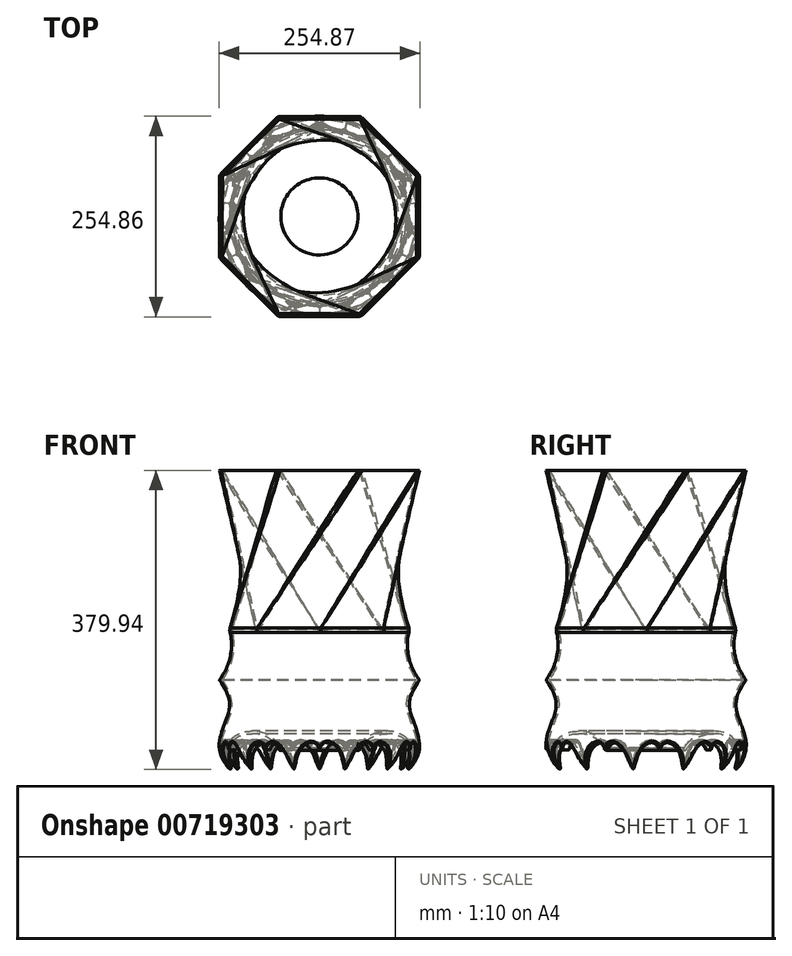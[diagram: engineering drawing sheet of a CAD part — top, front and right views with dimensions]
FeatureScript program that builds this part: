
annotation { "Feature Type Name" : "Feature", "Feature Type Description" : "" }
export const myFeature = defineFeature(function(context is Context, id is Id, definition is map)
    precondition{}
    {
        {
            var Q0;
            Q0=qCreatedBy(makeId("Front.planeOp"),FACE);
            var sketch = newSketch(context, id + "F0", { "sketchPlane" : qUnion([Q0])});
            skLineSegment(sketch, "E0", {"start": v(-49.67, 0) * mm, "end": v(1.13, 0) * mm});
            skLineSegment(sketch, "E1", {"start": v(-49.67, 0) * mm, "end": v(-49.67, 88.9) * mm});
            skLineSegment(sketch, "E2", {"start": v(-49.67, 88.9) * mm, "end": v(77.33, 88.9) * mm});
            skFitSpline(sketch, "E3", {"points": [v(77.33, 88.9) * mm, v(69.32, 37.63) * mm, v(77.33, 0) * mm, v(60.87, -29.47) * mm], "startDerivative": vector(-145.93, -197.22) * mm, "endDerivative": vector(-71.47, -73.7) * mm});
            skFitSpline(sketch, "E4", {"points": [v(1.13, 0) * mm, v(20.7, 18.23) * mm, v(52.43, 17.54) * mm, v(65.67, 0) * mm, v(60.87, -29.47) * mm], "startDerivative": vector(49.37, 90.75) * mm, "endDerivative": vector(-45.51, -125.15) * mm});
            skLineSegment(sketch, "E5", {"start": v(-49.67, 88.9) * mm, "end": v(-49.67, 152.4) * mm});
            skLineSegment(sketch, "E6", {"start": v(-49.67, 152.4) * mm, "end": v(64.63, 152.4) * mm});
            skFitSpline(sketch, "E7", {"points": [v(64.63, 152.4) * mm, v(64.63, 114.98) * mm, v(77.33, 88.9) * mm], "startDerivative": vector(-25.46, -92) * mm, "endDerivative": vector(52.49, -80.1) * mm});
            skSolve(sketch);
        }
        {
            var Q0;
            Q0=makeQuery(id+"F0.imprint","IMPRINT",FACE,{"disambiguationData":[TD([[makeQuery(id+"F0.imprint","IMPRINT",EDGE,{"derivedFrom":sQuery(id+"F0.wireOp",EDGE,"E0")}),1.0]])]});
            var Q1;
            Q1=makeQuery(id+"F0.imprint","IMPRINT",FACE,{"disambiguationData":[TD([[makeQuery(id+"F0.imprint","IMPRINT",EDGE,{"derivedFrom":sQuery(id+"F0.wireOp",EDGE,"E2")}),1.0]])]});
            var Q2;
            Q2=sQuery(id+"F0.wireOp",EDGE,"E1");
            revolve(context, id + "F1", {"surfaceOperationType" : NewSurfaceOperationType.NEW, "entities" : qUnion([Q0, Q1]), "axis" : qUnion([Q2]), "revolveType" : RevolveType.FULL});
        }
        {
            var Q0;
            Q0=qCreatedBy(makeId("Front.planeOp"),FACE);
            cPlane(context, id + "F2", {"entities" : qUnion([Q0]), "cplaneType" : CPlaneType.OFFSET, "offset" : 228.6 * mm, "width" : 152.4 * mm, "height" : 152.4 * mm});
        }
        {
            var Q0;
            Q0=qCreatedBy(id+"F2.planeOp",FACE);
            var sketch = newSketch(context, id + "F3", { "sketchPlane" : qUnion([Q0])});
            skLineSegment(sketch, "E8", {"start": v(-49.7, 40.01) * mm, "end": v(-49.7, -29.84) * mm});
            skLineSegment(sketch, "E9", {"start": v(-49.7, -29.84) * mm, "end": v(-14.14, -29.84) * mm});
            skFitSpline(sketch, "E10", {"points": [v(-14.14, -29.84) * mm, v(-16.53, -26.64) * mm, v(-19.6, -16.08) * mm, v(-22.29, -5.53) * mm, v(-27.66, 3.59) * mm, v(-36.85, 9.42) * mm, v(-49.7, 0.42) * mm], "startDerivative": vector(-16.59, 0) * mm, "endDerivative": vector(-32.26, -130.4) * mm});
            skFitSpline(sketch, "E11.MirrorCS", {"points": [v(-85.26, -29.84) * mm, v(-82.88, -26.64) * mm, v(-79.8, -16.08) * mm, v(-77.12, -5.53) * mm, v(-71.75, 3.59) * mm, v(-62.56, 9.42) * mm, v(-49.7, 0.42) * mm], "startDerivative": vector(16.59, 0) * mm, "endDerivative": vector(32.26, -130.4) * mm});
            skLineSegment(sketch, "E12.MirrorCS", {"start": v(-49.7, -29.84) * mm, "end": v(-85.26, -29.84) * mm});
            skSolve(sketch);
        }
        {
            var Q0;
            {var subQ0=sQuery(id+"F3.wireOp",EDGE,"E9");Q0=makeQuery(id+"F3.imprint","IMPRINT",FACE,{"disambiguationData":[TD([[makeQuery(id+"F3.imprint","IMPRINT",EDGE,{"derivedFrom":subQ0}),1.0]])]});}
            var Q1;
            {var subQ2=sQuery(id+"F3.wireOp",EDGE,"E11.MirrorCS");Q1=makeQuery(id+"F3.imprint","IMPRINT",FACE,{"disambiguationData":[TD([[makeQuery(id+"F3.imprint","IMPRINT",EDGE,{"derivedFrom":subQ2}),-1.0]])]});}
            extrude(context, id + "F4", {"entities" : qUnion([Q0, Q1]), "oppositeDirection" : true, "depth" : 152.4 * mm, "offsetDistance" : 25.4 * mm});
        }
        {
            var Q0;
            Q0=makeQuery(id+"F4.opExtrude","SWEPT_BODY",BODY,{"disambiguationData":[OSD([sQuery(id+"F3.wireOp",EDGE,"E9"),sQuery(id+"F3.wireOp",EDGE,"E10"),sQuery(id+"F3.wireOp",EDGE,"E11.MirrorCS"),sQuery(id+"F3.wireOp",EDGE,"E12.MirrorCS")])]});
            var Q1;
            Q1=sQuery(id+"F0.wireOp",EDGE,"E1");
            circularPattern(context, id + "F5", {"operationType" : NewBodyOperationType.REMOVE, "entities" : qUnion([Q0]), "axis" : qUnion([Q1]), "angle" : 360 * degree, "instanceCount" : 11, "equalSpace" : true});
        }
        {
            var Q0;
            Q0=qCreatedBy(makeId("Top.planeOp"),FACE);
            cPlane(context, id + "F6", {"entities" : qUnion([Q0]), "cplaneType" : CPlaneType.OFFSET, "offset" : 355.6 * mm, "width" : 152.4 * mm, "height" : 152.4 * mm});
        }
        {
            var Q0;
            Q0=qCreatedBy(id+"F6.planeOp",FACE);
            var sketch = newSketch(context, id + "F7", { "sketchPlane" : qUnion([Q0])});
            skCircle(sketch, "E13", {"center": v(-49.67, 0) * mm, "radius": 127 * mm, "construction": true});
            skLineSegment(sketch, "E14.0", {"start": v(2.93, 127) * mm, "end": v(77.33, 52.6) * mm});
            skLineSegment(sketch, "E14.1", {"start": v(77.33, 52.6) * mm, "end": v(77.33, -52.6) * mm});
            skLineSegment(sketch, "E14.2", {"start": v(77.33, -52.6) * mm, "end": v(2.93, -127) * mm});
            skLineSegment(sketch, "E14.3", {"start": v(2.93, -127) * mm, "end": v(-102.28, -127) * mm});
            skLineSegment(sketch, "E14.4", {"start": v(-102.28, -127) * mm, "end": v(-176.67, -52.6) * mm});
            skLineSegment(sketch, "E14.5", {"start": v(-176.67, -52.6) * mm, "end": v(-176.67, 52.6) * mm});
            skLineSegment(sketch, "E14.6", {"start": v(-176.67, 52.6) * mm, "end": v(-102.28, 127) * mm});
            skLineSegment(sketch, "E14.7", {"start": v(-102.28, 127) * mm, "end": v(2.93, 127) * mm});
            skPoint(sketch, "E14.0.midPoint", {"position": v(40.13, 89.8) * mm});
            skPoint(sketch, "E15", {"position": v(-49.67, 127) * mm});
            skSolve(sketch);
        }
        {
            var Q0;
            Q0=makeQuery(id+"F1.opRevolve","SWEPT_FACE",FACE,{"disambiguationData":[OSD([sQuery(id+"F0.wireOp",EDGE,"E6")])]});
            var sketch = newSketch(context, id + "F8", { "sketchPlane" : qUnion([Q0])});
            skCircle(sketch, "E16", {"center": v(-49.67, 0) * mm, "radius": 114.3 * mm});
            skPoint(sketch, "E17", {"position": v(-49.67, 114.3) * mm});
            skSolve(sketch);
        }
        {
            var Q0;
            Q0=sQuery(id+"F7.wireOp",VERTEX,"E15");
            var Q1;
            Q1=sQuery(id+"F8.wireOp",VERTEX,"E17");
            var Q2;
            Q2=sQuery(id+"F7.wireOp",VERTEX,"E14.6.start");
            cPlane(context, id + "F9", {"entities" : qUnion([Q0, Q1, Q2]), "cplaneType" : CPlaneType.THREE_POINT, "offset" : 25.4 * mm, "width" : 152.4 * mm, "height" : 152.4 * mm});
        }
        {
            var Q0;
            Q0=qCreatedBy(id+"F9.planeOp",FACE);
            var sketch = newSketch(context, id + "F10", { "sketchPlane" : qUnion([Q0])});
            skLineSegment(sketch, "E18", {"start": v(9.9, 159.23) * mm, "end": v(-137.22, 358.19) * mm});
            skSolve(sketch);
        }
        {
            var Q0;
            Q0 = qSketchRegion(id + "F7", true);
            var Q1;
            Q1 = qSketchRegion(id + "F8", true);
            var Q2;
            Q2 = qConstructionFilter(qBodyType(qCreatedBy(id + "F10" ,EDGE), BodyType.WIRE), ConstructionObject.NO);
            loft(context, id + "F11", {"operationType" : NewBodyOperationType.ADD, "addGuides" : true, "sheetProfilesArray" : [{ "sheetProfileEntities" : qUnion([Q0]) }, { "sheetProfileEntities" : qUnion([Q1]) }], "guidesArray" : [{ "guideEntities" : qUnion([Q2]), "guideDerivativeType" : LoftGuideDerivativeType.DEFAULT, "guideDerivativeMagnitude" : 1 }]});
        }
        {
            var Q0;
            Q0=makeQuery(id+"F1.opRevolve","SWEPT_EDGE",EDGE,{"disambiguationData":[OSD([sQuery(id+"F0.wireOp",EDGE,"E6"),sQuery(id+"F0.wireOp",EDGE,"E7")])]});
            fillet(context, id + "F12", {"entities" : qUnion([Q0]), "radius" : 10.16 * mm, "tangentPropagation" : true, "allowEdgeOverflow" : false});
        }
        {
            var Q0;
            Q0=makeQuery(id+"F1.opRevolve","SWEPT_EDGE",EDGE,{"disambiguationData":[OSD([sQuery(id+"F0.wireOp",EDGE,"E2"),sQuery(id+"F0.wireOp",EDGE,"E3"),sQuery(id+"F0.wireOp",EDGE,"E7")])]});
            var Q1;
            Q1=makeQuery(id+"F1.opRevolve","SWEPT_FACE",FACE,{"disambiguationData":[OSD([sQuery(id+"F0.wireOp",EDGE,"E3")])]});
            var Q2;
            Q2=makeQuery(id+"F1.opRevolve","SWEPT_FACE",FACE,{"disambiguationData":[OSD([sQuery(id+"F0.wireOp",EDGE,"E4")])]});
            fillet(context, id + "F13", {"entities" : qUnion([Q0, Q1, Q2]), "radius" : 1.27 * mm, "tangentPropagation" : true, "allowEdgeOverflow" : false});
        }
        {
            var Q0;
            Q0=makeQuery(id+"F11.opLoft","CAP_FACE",FACE,{"disambiguationData":[OSD([makeQuery(id+"F7.imprint","IMPRINT",FACE,{"disambiguationData":[TD([[makeQuery(id+"F7.imprint","IMPRINT",EDGE,{"derivedFrom":sQuery(id+"F7.wireOp",EDGE,"E14.0")}),-1.0]])]})])],"isStart":true});
            shell(context, id + "F14", {"entities" : qUnion([Q0]), "thickness" : 3.2 * mm});
        }
        {
            var Q0;
            Q0=makeQuery(id+"F11.opLoft","SWEPT_EDGE",EDGE,{"disambiguationData":[OSD([sQuery(id+"F7.wireOp",EDGE,"E14.1"),sQuery(id+"F7.wireOp",EDGE,"E14.2"),sQuery(id+"F7.wireOp",EDGE,"E14.3"),sQuery(id+"F8.wireOp",EDGE,"E16")])]});
            var Q1;
            Q1=makeQuery(id+"F11.opLoft","SWEPT_EDGE",EDGE,{"disambiguationData":[OSD([sQuery(id+"F7.wireOp",EDGE,"E14.0"),sQuery(id+"F7.wireOp",EDGE,"E14.1"),sQuery(id+"F7.wireOp",EDGE,"E14.2"),sQuery(id+"F8.wireOp",EDGE,"E16")])]});
            var Q2;
            Q2=makeQuery(id+"F11.opLoft","SWEPT_EDGE",EDGE,{"disambiguationData":[OSD([sQuery(id+"F7.wireOp",EDGE,"E14.0"),sQuery(id+"F7.wireOp",EDGE,"E14.1"),sQuery(id+"F7.wireOp",EDGE,"E14.7"),sQuery(id+"F8.wireOp",EDGE,"E16")])]});
            var Q3;
            Q3=makeQuery(id+"F11.opLoft","SWEPT_EDGE",EDGE,{"disambiguationData":[OSD([sQuery(id+"F7.wireOp",EDGE,"E14.0"),sQuery(id+"F7.wireOp",EDGE,"E14.6"),sQuery(id+"F7.wireOp",EDGE,"E14.7"),sQuery(id+"F8.wireOp",EDGE,"E16")])]});
            var Q4;
            Q4=makeQuery(id+"F11.opLoft","SWEPT_EDGE",EDGE,{"disambiguationData":[OSD([sQuery(id+"F7.wireOp",EDGE,"E14.6"),sQuery(id+"F7.wireOp",EDGE,"E14.7"),sQuery(id+"F8.wireOp",EDGE,"E16"),sQuery(id+"F10.wireOp",EDGE,"E18")])]});
            var Q5;
            Q5=makeQuery(id+"F11.opLoft","SWEPT_EDGE",EDGE,{"disambiguationData":[OSD([sQuery(id+"F10.wireOp",EDGE,"E18")])]});
            var Q6;
            Q6=makeQuery(id+"F11.opLoft","SWEPT_EDGE",EDGE,{"disambiguationData":[OSD([sQuery(id+"F7.wireOp",EDGE,"E14.3"),sQuery(id+"F7.wireOp",EDGE,"E14.4"),sQuery(id+"F7.wireOp",EDGE,"E14.5"),sQuery(id+"F8.wireOp",EDGE,"E16")])]});
            var Q7;
            Q7=makeQuery(id+"F11.opLoft","SWEPT_EDGE",EDGE,{"disambiguationData":[OSD([sQuery(id+"F7.wireOp",EDGE,"E14.2"),sQuery(id+"F7.wireOp",EDGE,"E14.3"),sQuery(id+"F7.wireOp",EDGE,"E14.4"),sQuery(id+"F8.wireOp",EDGE,"E16")])]});
            fillet(context, id + "F15", {"entities" : qUnion([Q0, Q1, Q2, Q3, Q4, Q5, Q6, Q7]), "radius" : 6.35 * mm, "tangentPropagation" : true, "allowEdgeOverflow" : false});
        }
    });
